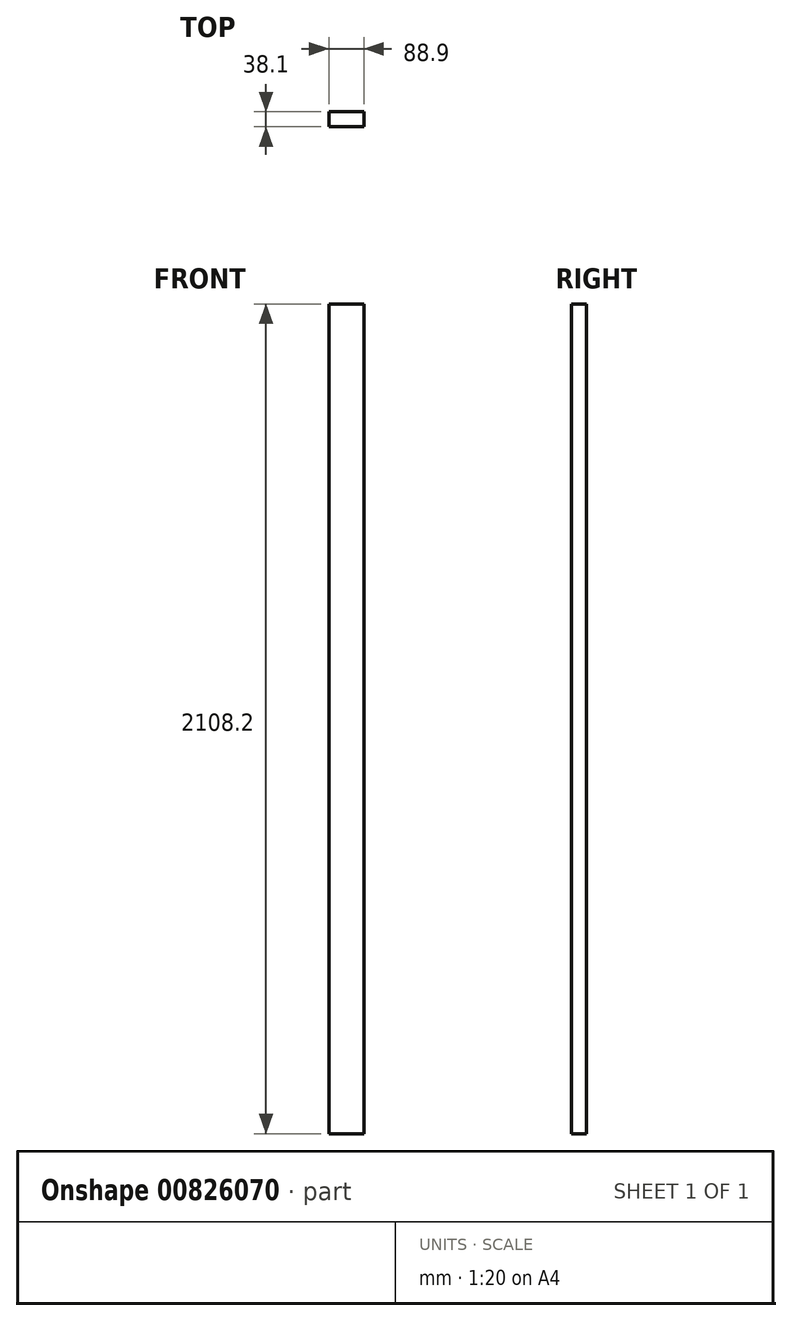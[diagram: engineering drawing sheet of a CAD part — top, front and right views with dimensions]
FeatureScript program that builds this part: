
annotation { "Feature Type Name" : "Feature", "Feature Type Description" : "" }
export const myFeature = defineFeature(function(context is Context, id is Id, definition is map)
    precondition{}
    {
        {
            var Q0;
            Q0=qCreatedBy(makeId("Top.planeOp"),FACE);
            var sketch = newSketch(context, id + "F0", { "sketchPlane" : qUnion([Q0])});
            skLineSegment(sketch, "E0.bottom", {"start": v(0, 0) * mm, "end": v(88.9, 0) * mm});
            skLineSegment(sketch, "E0.top", {"start": v(0, 38.1) * mm, "end": v(88.9, 38.1) * mm});
            skLineSegment(sketch, "E0.left", {"start": v(0, 0) * mm, "end": v(0, 38.1) * mm});
            skLineSegment(sketch, "E0.right", {"start": v(88.9, 0) * mm, "end": v(88.9, 38.1) * mm});
            skSolve(sketch);
        }
        {
            var Q0;
            Q0=qSketchRegion(id+"F0",true);
            extrude(context, id + "F1", {"entities" : qUnion([Q0]), "depth" : 2108.2 * mm, "offsetDistance" : 25.4 * mm});
        }
    });
